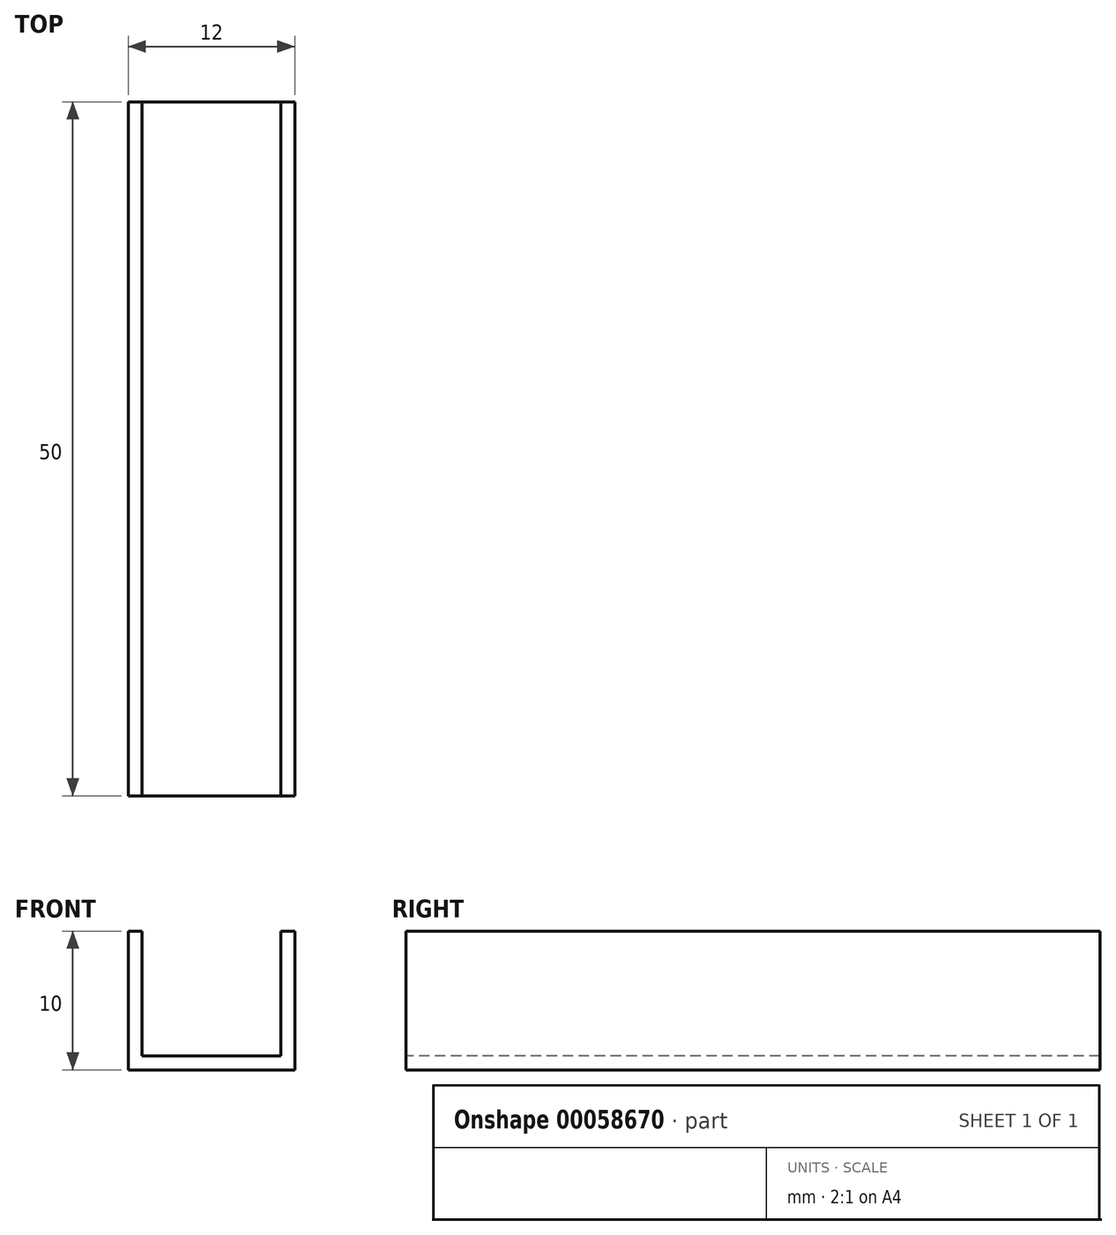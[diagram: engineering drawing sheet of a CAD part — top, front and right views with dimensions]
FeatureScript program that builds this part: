
annotation { "Feature Type Name" : "Feature", "Feature Type Description" : "" }
export const myFeature = defineFeature(function(context is Context, id is Id, definition is map)
    precondition{}
    {
        {
            var Q0;
            Q0=qCreatedBy(makeId("Top.planeOp"),FACE);
            var sketch = newSketch(context, id + "F0", { "sketchPlane" : qUnion([Q0])});
            skLineSegment(sketch, "E0.rect.bottom", {"start": v(-5, 25) * mm, "end": v(5, 25) * mm});
            skLineSegment(sketch, "E0.rect.top", {"start": v(-5, -25) * mm, "end": v(5, -25) * mm});
            skLineSegment(sketch, "E0.rect.left", {"start": v(-5, 25) * mm, "end": v(-5, -25) * mm});
            skLineSegment(sketch, "E0.rect.right", {"start": v(5, 25) * mm, "end": v(5, -25) * mm});
            skPoint(sketch, "E0.rect.middle", {"position": v(0, 0) * mm});
            skLineSegment(sketch, "E1.bottom", {"start": v(5, -25) * mm, "end": v(6, -25) * mm});
            skLineSegment(sketch, "E1.top", {"start": v(5, 25) * mm, "end": v(6, 25) * mm});
            skLineSegment(sketch, "E1.left", {"start": v(5, -25) * mm, "end": v(5, 25) * mm});
            skLineSegment(sketch, "E1.right", {"start": v(6, -25) * mm, "end": v(6, 25) * mm});
            skLineSegment(sketch, "E2.bottom", {"start": v(-5, -25) * mm, "end": v(-6, -25) * mm});
            skLineSegment(sketch, "E2.top", {"start": v(-5, 25) * mm, "end": v(-6, 25) * mm});
            skLineSegment(sketch, "E2.left", {"start": v(-5, -25) * mm, "end": v(-5, 25) * mm});
            skLineSegment(sketch, "E2.right", {"start": v(-6, -25) * mm, "end": v(-6, 25) * mm});
            skSolve(sketch);
        }
        {
            var Q0;
            Q0=makeQuery(id+"F0.imprint","IMPRINT",FACE,{"disambiguationData":[TD([[makeQuery(id+"F0.imprint","IMPRINT",EDGE,{"derivedFrom":sQuery(id+"F0.wireOp",EDGE,"E0.rect.bottom")}),-1.0]])]});
            extrude(context, id + "F1", {"entities" : qUnion([Q0]), "depth" : 1 * mm});
        }
        {
            var Q0;
            Q0=makeQuery(id+"F0.imprint","IMPRINT",FACE,{"disambiguationData":[TD([[makeQuery(id+"F0.imprint","IMPRINT",EDGE,{"derivedFrom":sQuery(id+"F0.wireOp",EDGE,"E2.bottom")}),-1.0]])]});
            var Q1;
            Q1=makeQuery(id+"F0.imprint","IMPRINT",FACE,{"disambiguationData":[TD([[makeQuery(id+"F0.imprint","IMPRINT",EDGE,{"derivedFrom":sQuery(id+"F0.wireOp",EDGE,"E1.bottom")}),1.0]])]});
            extrude(context, id + "F2", {"entities" : qUnion([Q0, Q1]), "operationType" : NewBodyOperationType.ADD, "depth" : 10 * mm});
        }
    });
